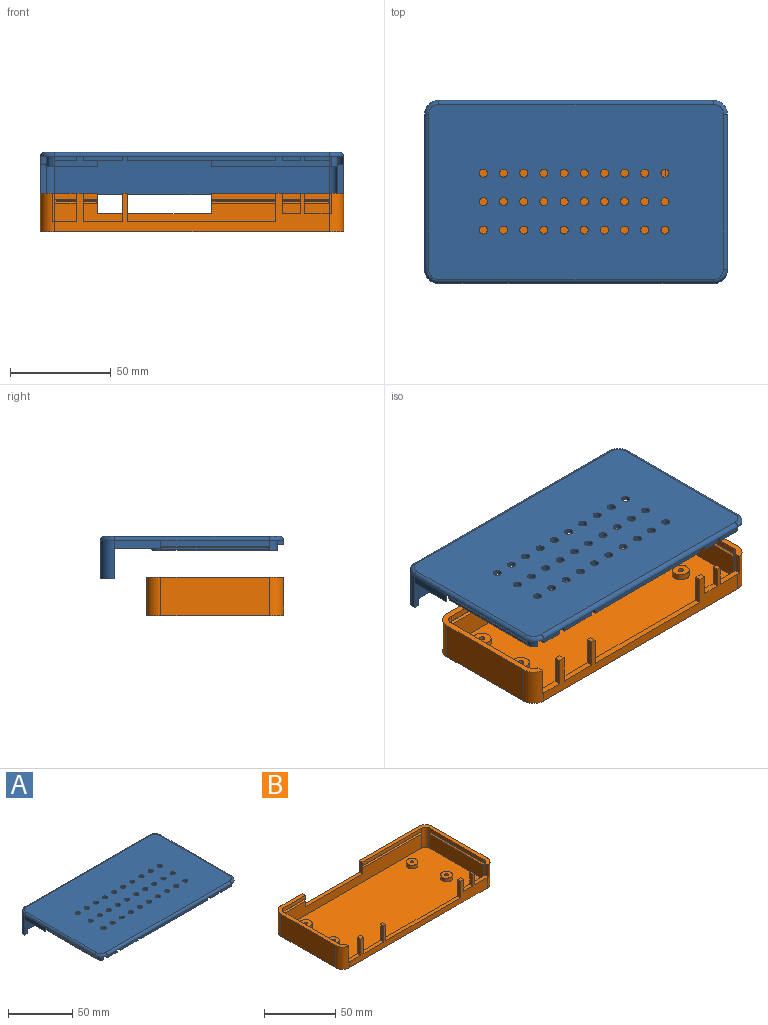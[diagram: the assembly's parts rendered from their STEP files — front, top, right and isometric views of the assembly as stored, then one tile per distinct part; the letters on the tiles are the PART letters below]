
ASSEMBLY  parts=2 mates=1
PART A: 124 faces, bbox 151.4x91.9x21 mm
  f0: plane 12.25x2mm, normal (0,-1,0), area 24.5mm2, adj f74,f75,f76,f118
  f1: plane 8.94x2mm, normal (0,-1,0), area 17.9mm2, adj f82,f83,f84,f118
  f2: plane 73.55x2mm, normal (0,-1,0), area 147.1mm2, adj f66,f67,f68,f118
  f3: plane 19.47x2mm, normal (0,-1,0), area 38.9mm2, adj f70,f71,f72,f118
  f4: plane 23x4mm, normal (-1,0,0), area 92mm2, adj f7,f97,f113,f122
  f5: plane 17.2x4mm, normal (1,0,0), area 68.8mm2, adj f7,f11,f98,f113
  f6: plane 17.2x4mm, normal (-1,0,0), area 68.8mm2, adj f8,f11,f100,f115
  f7: cylinder r=7.1mm len=5.8mm, axis (0,0,1), area 27.1mm2, adj f4,f5,f11,f113
  f8: cylinder r=7.1mm len=5.8mm, axis (0,0,1), area 27.1mm2, adj f6,f11,f13,f115
  f9: plane 53.67x3mm, normal (1,0,0), area 161mm2, adj f11,f47,f48,f91
  f10: plane 53.67x3mm, normal (-1,0,0), area 161mm2, adj f11,f62,f63,f85
  f11: plane 150.25x87.77mm, normal (0,0,-1), area 12041mm2, adj f5,f6,f7,f8,f9,f10,f14,f15
  f12: plane 10.91x2mm, normal (0,-1,0), area 21.8mm2, adj f78,f79,f80,f118
  f13: plane 23x4mm, normal (1,0,0), area 92mm2, adj f8,f95,f115,f117
  f14: cylinder r=2mm len=4mm, axis (0,0,-1), area 25.1mm2, adj f11,f44
  f15: cylinder r=2mm len=4mm, axis (0,0,-1), area 25.1mm2, adj f11,f44
  f16: cylinder r=2mm len=4mm, axis (0,0,-1), area 25.1mm2, adj f11,f44
  f17: cylinder r=2mm len=4mm, axis (0,0,-1), area 25.1mm2, adj f11,f44
  f18: cylinder r=2mm len=4mm, axis (0,0,-1), area 25.1mm2, adj f11,f44
  f19: cylinder r=2mm len=4mm, axis (0,0,-1), area 25.1mm2, adj f11,f44
  f20: cylinder r=2mm len=4mm, axis (0,0,-1), area 25.1mm2, adj f11,f44
  f21: cylinder r=2mm len=4mm, axis (0,0,-1), area 25.1mm2, adj f11,f44
  f22: cylinder r=2mm len=4mm, axis (0,0,-1), area 25.1mm2, adj f11,f44
  f23: cylinder r=2mm len=4mm, axis (0,0,-1), area 25.1mm2, adj f11,f44
  f24: cylinder r=2mm len=4mm, axis (0,0,-1), area 25.1mm2, adj f11,f44
  f25: cylinder r=2mm len=4mm, axis (0,0,-1), area 25.1mm2, adj f11,f44
  f26: cylinder r=2mm len=4mm, axis (0,0,-1), area 25.1mm2, adj f11,f44
  f27: cylinder r=2mm len=4mm, axis (0,0,-1), area 25.1mm2, adj f11,f44
  f28: cylinder r=2mm len=4mm, axis (0,0,-1), area 25.1mm2, adj f11,f44
  f29: cylinder r=2mm len=4mm, axis (0,0,-1), area 25.1mm2, adj f11,f44
  f30: cylinder r=2mm len=4mm, axis (0,0,-1), area 25.1mm2, adj f11,f44
  f31: cylinder r=2mm len=4mm, axis (0,0,-1), area 25.1mm2, adj f11,f44
  f32: cylinder r=2mm len=4mm, axis (0,0,-1), area 25.1mm2, adj f11,f44
  f33: cylinder r=2mm len=4mm, axis (0,0,-1), area 25.1mm2, adj f11,f44
  f34: cylinder r=2mm len=4mm, axis (0,0,-1), area 25.1mm2, adj f11,f44
  f35: cylinder r=2mm len=4mm, axis (0,0,-1), area 25.1mm2, adj f11,f44
  f36: cylinder r=2mm len=4mm, axis (0,0,-1), area 25.1mm2, adj f11,f44
  f37: cylinder r=2mm len=4mm, axis (0,0,-1), area 25.1mm2, adj f11,f44
  f38: cylinder r=2mm len=4mm, axis (0,0,-1), area 25.1mm2, adj f11,f44
  f39: cylinder r=2mm len=4mm, axis (0,0,-1), area 25.1mm2, adj f11,f44
  f40: cylinder r=2mm len=4mm, axis (0,0,-1), area 25.1mm2, adj f11,f44
  f41: cylinder r=2mm len=4mm, axis (0,0,-1), area 25.1mm2, adj f11,f44
  f42: cylinder r=2mm len=4mm, axis (0,0,-1), area 25.1mm2, adj f11,f44
  f43: cylinder r=2mm len=4mm, axis (0,0,-1), area 25.1mm2, adj f11,f44
  f44: plane 146.25x86.77mm, normal (0,0,1), area 12290.9mm2, adj f14,f15,f16,f17,f18,f19,f20,f21
  f45: cylinder r=3mm len=5mm, axis (0,0,1), area 17mm2, adj f11,f46,f53,f54
  f46: plane 5x1.18mm, normal (-1,0,0), area 5.9mm2, adj f11,f45,f47,f54
  f47: cylinder r=4.1mm len=5mm, axis (0,0,1), area 25.7mm2, adj f9,f11,f46,f54,f92
  f48: cylinder r=4.1mm len=5mm, axis (0,0,1), area 32.2mm2, adj f9,f11,f49,f54,f90
  f49: plane 58.46x5mm, normal (0,1,0), area 217.5mm2, adj f11,f48,f50,f54,f103,f104
  f50: plane 5x1.1mm, normal (-1,0,0), area 5.5mm2, adj f11,f49,f51,f54,f102
  f51: plane 58.46x5mm, normal (0,-1,0), area 292.3mm2, adj f11,f50,f52,f54
  f52: cylinder r=3mm len=5mm, axis (0,0,1), area 23.6mm2, adj f11,f51,f53,f54
  f53: plane 53.67x5mm, normal (-1,0,0), area 268.4mm2, adj f11,f45,f52,f54
  f54: plane 62.56x61.67mm, normal (0,0,-1), area 134.2mm2, adj f45,f46,f47,f48,f49,f50,f51,f52
  f55: plane 5x1.14mm, normal (1,0,0), area 5.7mm2, adj f11,f56,f63,f64
  f56: cylinder r=3mm len=5mm, axis (0,0,1), area 18.7mm2, adj f11,f55,f57,f64
  f57: plane 53.67x5mm, normal (1,0,0), area 268.4mm2, adj f11,f56,f58,f64
  f58: cylinder r=3mm len=5mm, axis (0,0,1), area 23.6mm2, adj f11,f57,f59,f64
  f59: plane 21.13x5mm, normal (0,-1,0), area 105.6mm2, adj f11,f58,f60,f64
  f60: plane 5x1.1mm, normal (1,0,0), area 5.5mm2, adj f11,f59,f61,f64
  f61: plane 21.13x5mm, normal (0,1,0), area 74.7mm2, adj f11,f60,f62,f64,f107,f109,f110
  f62: cylinder r=4.1mm len=5mm, axis (0,0,1), area 32.2mm2, adj f10,f11,f61,f64,f86
  f63: cylinder r=4.1mm len=5mm, axis (0,0,1), area 27.4mm2, adj f10,f11,f55,f64,f88
  f64: plane 61.76x25.23mm, normal (0,0,-1), area 93.5mm2, adj f55,f56,f57,f58,f59,f60,f61,f62
  f65: plane 73.55x2mm, normal (0,1,0), area 147.1mm2, adj f11,f66,f67,f68
  f66: plane 3x2mm, normal (-1,0,0), area 6mm2, adj f2,f11,f65,f68
  f67: plane 3x2mm, normal (1,0,0), area 6mm2, adj f2,f11,f65,f68
  f68: plane 73.55x3mm, normal (0,0,-1), area 220.7mm2, adj f2,f65,f66,f67
  f69: plane 19.47x2mm, normal (0,1,0), area 38.9mm2, adj f11,f70,f71,f72
  f70: plane 3x2mm, normal (-1,0,0), area 6mm2, adj f3,f11,f69,f72
  f71: plane 3x2mm, normal (1,0,0), area 6mm2, adj f3,f11,f69,f72
  f72: plane 19.47x3mm, normal (0,0,-1), area 58.4mm2, adj f3,f69,f70,f71
  f73: plane 12.25x2mm, normal (0,1,0), area 24.5mm2, adj f11,f74,f75,f76
  f74: plane 3x2mm, normal (-1,0,0), area 6mm2, adj f0,f11,f73,f76
  f75: plane 3x2mm, normal (1,0,0), area 6mm2, adj f0,f11,f73,f76
  f76: plane 12.25x3mm, normal (0,0,-1), area 36.8mm2, adj f0,f73,f74,f75
  f77: plane 10.91x2mm, normal (0,1,0), area 21.8mm2, adj f11,f78,f79,f80
  f78: plane 3x2mm, normal (-1,0,0), area 6mm2, adj f11,f12,f77,f80
  f79: plane 3x2mm, normal (1,0,0), area 6mm2, adj f11,f12,f77,f80
  f80: plane 10.91x3mm, normal (0,0,-1), area 32.7mm2, adj f12,f77,f78,f79
  f81: plane 8.94x2mm, normal (0,1,0), area 17.9mm2, adj f11,f82,f83,f84
  f82: plane 3x2mm, normal (-1,0,0), area 6mm2, adj f1,f11,f81,f84
  f83: plane 3x2mm, normal (1,0,0), area 6mm2, adj f1,f11,f81,f84
  f84: plane 8.94x3mm, normal (0,0,-1), area 26.8mm2, adj f1,f81,f82,f83
  f85: plane 53.67x0.5mm, normal (-0.64,0,0.77), area 34.8mm2, adj f10,f86,f88,f89
  f86: plane 2x0.5mm, normal (-0.64,0.77,0), area 1mm2, adj f62,f85,f87,f89
  f87: plane 53.67x0.5mm, normal (-0.64,0,-0.77), area 34.8mm2, adj f64,f86,f88,f89
  f88: plane 2x0.5mm, normal (-0.64,-0.77,0), area 1mm2, adj f63,f85,f87,f89
  f89: plane 52.83x1.16mm, normal (-1,0,0), area 61.3mm2, adj f85,f86,f87,f88
  f90: plane 2x0.5mm, normal (0.64,0.77,0), area 1mm2, adj f48,f91,f93,f94
  f91: plane 53.67x0.5mm, normal (0.64,0,0.77), area 34.8mm2, adj f9,f90,f92,f94
  f92: plane 2x0.5mm, normal (0.64,-0.77,0), area 1mm2, adj f47,f91,f93,f94
  f93: plane 53.67x0.5mm, normal (0.64,0,-0.77), area 34.8mm2, adj f54,f90,f92,f94
  f94: plane 52.83x1.16mm, normal (1,0,0), area 61.3mm2, adj f90,f91,f92,f93
  f95: cylinder r=7mm len=19mm, axis (0,0,1), area 208.9mm2, adj f13,f96,f101,f114,f119
  f96: plane 136.25x19mm, normal (0,1,0), area 2588.7mm2, adj f95,f97,f101,f121
  f97: cylinder r=7mm len=19mm, axis (0,0,1), area 208.9mm2, adj f4,f96,f101,f112,f123
  f98: cylinder r=4mm len=19mm, axis (0,0,1), area 119.4mm2, adj f5,f11,f99,f101,f112
  f99: plane 136.25x19mm, normal (0,-1,0), area 2588.7mm2, adj f11,f98,f100,f101
  f100: cylinder r=4mm len=19mm, axis (0,0,1), area 119.4mm2, adj f6,f11,f99,f101,f114
  f101: plane 150.25x7mm, normal (0,0,-1), area 460.6mm2, adj f95,f96,f97,f98,f99,f100,f112,f114
  f102: plane 2x0.5mm, normal (-0.77,0.64,0), area 1mm2, adj f50,f103,f105,f106
  f103: plane 37.38x0.5mm, normal (0,0.64,0.77), area 24.1mm2, adj f49,f102,f104,f106
  f104: plane 2x0.5mm, normal (0.77,0.64,0), area 1mm2, adj f49,f103,f105,f106
  f105: plane 37.38x0.5mm, normal (0,0.64,-0.77), area 24.1mm2, adj f54,f102,f104,f106
  f106: plane 36.54x1.16mm, normal (0,1,0), area 42.4mm2, adj f102,f103,f104,f105
  f107: plane 2x0.5mm, normal (0.77,0.64,0), area 1mm2, adj f61,f108,f110,f111
  f108: plane 15.48x0.5mm, normal (0,0.64,-0.77), area 9.8mm2, adj f64,f107,f109,f111
  f109: plane 2x0.5mm, normal (-0.77,0.64,0), area 1mm2, adj f61,f108,f110,f111
  f110: plane 15.48x0.5mm, normal (0,0.64,0.77), area 9.8mm2, adj f61,f107,f109,f111
  f111: plane 14.64x1.16mm, normal (0,1,0), area 17mm2, adj f107,f108,f109,f110
  f112: plane 15x3mm, normal (0,-1,0), area 45mm2, adj f97,f98,f101,f113
  f113: plane 23x3mm, normal (0,0,-1), area 56.8mm2, adj f4,f5,f7,f112
  f114: plane 15x3mm, normal (0,-1,0), area 45mm2, adj f95,f100,f101,f115
  f115: plane 23x3mm, normal (0,0,-1), area 56.8mm2, adj f6,f8,f13,f114
  f116: torus R=5.1mm, axis (0,0,1), area 31.5mm2, adj f11,f44,f117,f118
  f117: cylinder r=2mm len=76.67mm, axis (0,-1,0), area 240.9mm2, adj f11,f13,f44,f116,f119
  f118: cylinder r=2mm len=136.05mm, axis (-1,0,0), area 427.4mm2, adj f0,f1,f2,f3,f11,f12,f44,f116
  f119: torus R=5mm, axis (0,0,1), area 31mm2, adj f44,f95,f117,f121
  f120: torus R=5.1mm, axis (0,0,1), area 31.5mm2, adj f11,f44,f118,f122
  f121: cylinder r=2mm len=136.25mm, axis (-1,0,0), area 428mm2, adj f44,f96,f119,f123
  f122: cylinder r=2mm len=76.67mm, axis (0,1,0), area 240.9mm2, adj f4,f11,f44,f120,f123
  f123: torus R=5mm, axis (0,0,1), area 31mm2, adj f44,f97,f121,f122
PART B: 78 faces, bbox 150.2x67.9x19 mm
  f0: plane 53.67x12mm, normal (1,0,0), area 644.1mm2, adj f4,f22,f24,f76
  f1: plane 53.67x12mm, normal (-1,0,0), area 644.1mm2, adj f4,f19,f26,f70
  f2: plane 136.05x12mm, normal (0,-1,0), area 1350.2mm2, adj f4,f24,f26,f42,f43,f44,f60,f65
  f3: plane 21.13x3mm, normal (0,-1,0), area 63.4mm2, adj f24,f28,f42,f63
  f4: plane 144.25x61.87mm, normal (0,0,1), area 8687.6mm2, adj f0,f1,f2,f19,f22,f24,f26,f29
  f5: plane 67.76x65.56mm, normal (0,0,1), area 385.3mm2, adj f8,f9,f10,f11,f19,f20,f25,f26
  f6: cylinder r=7.1mm len=19mm, axis (0,0,1), area 198.5mm2, adj f7,f16,f18,f21,f28,f47
  f7: plane 136.05x19mm, normal (0,-1,0), area 917.9mm2, adj f6,f8,f18,f30,f31,f32,f33,f34
  f8: cylinder r=7.1mm len=19mm, axis (0,0,1), area 199.1mm2, adj f5,f7,f9,f18,f20,f45
  f9: plane 53.67x19mm, normal (1,0,0), area 1019.7mm2, adj f5,f8,f10,f18
  f10: cylinder r=7.1mm len=19mm, axis (0,0,1), area 211.9mm2, adj f5,f9,f11,f18
  f11: plane 136.05x19mm, normal (0,1,0), area 2020.2mm2, adj f5,f10,f12,f18,f28,f42,f43,f44
  f12: cylinder r=7.1mm len=19mm, axis (0,0,1), area 211.9mm2, adj f11,f16,f18,f28
  f13: cylinder r=1.25mm len=5mm, axis (0,0,1), area 39.3mm2, adj f18,f53
  f14: cylinder r=1.25mm len=5mm, axis (0,0,1), area 39.3mm2, adj f18,f55
  f15: cylinder r=1.25mm len=5mm, axis (0,0,1), area 39.3mm2, adj f18,f57
  f16: plane 53.67x19mm, normal (-1,0,0), area 1019.7mm2, adj f6,f12,f18,f28
  f17: cylinder r=1.25mm len=5mm, axis (0,0,1), area 39.3mm2, adj f18,f51
  f18: plane 150.25x67.87mm, normal (0,0,-1), area 10134.4mm2, adj f6,f7,f8,f9,f10,f11,f12,f13
  f19: cylinder r=4.1mm len=17mm, axis (0,0,-1), area 96.5mm2, adj f1,f4,f5,f20,f27,f29,f45,f71
  f20: plane 10x3.09mm, normal (-1,0,0), area 30.9mm2, adj f5,f8,f19,f45
  f21: plane 14x3.05mm, normal (1,0,0), area 42.7mm2, adj f6,f22,f28,f47
  f22: cylinder r=4.1mm len=17mm, axis (0,0,-1), area 96mm2, adj f0,f4,f21,f23,f28,f29,f47,f75
  f23: plane 53.67x3mm, normal (1,0,0), area 161mm2, adj f22,f24,f28,f74
  f24: cylinder r=4.1mm len=17mm, axis (0,0,-1), area 109.5mm2, adj f0,f2,f3,f4,f23,f28,f64,f73
  f25: plane 58.46x3mm, normal (0,-1,0), area 175.4mm2, adj f5,f26,f43,f58
  f26: cylinder r=4.1mm len=17mm, axis (0,0,-1), area 109.5mm2, adj f1,f2,f4,f5,f25,f27,f61,f69
  f27: plane 53.67x3mm, normal (-1,0,0), area 161mm2, adj f5,f19,f26,f68
  f28: plane 67.81x28.23mm, normal (0,0,1), area 274.3mm2, adj f3,f6,f11,f12,f16,f21,f22,f23
  f29: plane 136.05x17mm, normal (0,1,0), area 645.8mm2, adj f4,f19,f22,f30,f31,f32,f33,f34
  f30: plane 14x3mm, normal (-1,0,0), area 42mm2, adj f7,f29,f32,f47
  f31: plane 14x3mm, normal (1,0,0), area 42mm2, adj f7,f29,f32,f49
  f32: plane 3.37x3mm, normal (0,0,1), area 10.1mm2, adj f7,f29,f30,f31
  f33: plane 14x3mm, normal (-1,0,0), area 42mm2, adj f7,f29,f35,f48
  f34: plane 10x3mm, normal (1,0,0), area 30mm2, adj f7,f29,f35,f46
  f35: plane 3.36x3mm, normal (0,0,1), area 10.1mm2, adj f7,f29,f33,f34
  f36: plane 14x3mm, normal (-1,0,0), area 42mm2, adj f7,f29,f38,f49
  f37: plane 14x3mm, normal (1,0,0), area 42mm2, adj f7,f29,f38,f48
  f38: plane 3x2.2mm, normal (0,0,1), area 6.6mm2, adj f7,f29,f36,f37
  f39: plane 10x3mm, normal (-1,0,0), area 30mm2, adj f7,f29,f41,f46
  f40: plane 10x3mm, normal (1,0,0), area 30mm2, adj f7,f29,f41,f45
  f41: plane 3x1.99mm, normal (0,0,1), area 6mm2, adj f7,f29,f39,f40
  f42: plane 10x3mm, normal (1,0,0), area 30mm2, adj f2,f3,f11,f28,f44,f66
  f43: plane 10x3mm, normal (-1,0,0), area 30mm2, adj f2,f5,f11,f25,f44,f59
  f44: plane 56.46x3mm, normal (0,0,1), area 169.4mm2, adj f2,f11,f42,f43
  f45: plane 13.53x3.2mm, normal (0,0,1), area 40.6mm2, adj f7,f8,f19,f20,f29,f40
  f46: plane 8.94x3mm, normal (0,0,1), area 26.8mm2, adj f7,f29,f34,f39
  f47: plane 11.87x3.11mm, normal (0,0,1), area 35.6mm2, adj f6,f7,f21,f22,f29,f30
  f48: plane 73.55x3mm, normal (0,0,1), area 220.7mm2, adj f7,f29,f33,f37
  f49: plane 19.47x3mm, normal (0,0,1), area 58.4mm2, adj f7,f29,f31,f36
  f50: cylinder r=4.38mm len=8.76mm, axis (0,0,-1), area 82.5mm2, adj f4,f51
  f51: plane 8.76x8.76mm, normal (0,0,1), area 55.3mm2, adj f17,f50
  f52: cylinder r=4.15mm len=8.3mm, axis (0,0,-1), area 78.2mm2, adj f4,f53
  f53: plane 8.3x8.3mm, normal (0,0,1), area 49.2mm2, adj f13,f52
  f54: cylinder r=4.15mm len=8.3mm, axis (0,0,-1), area 78.2mm2, adj f4,f55
  f55: plane 8.3x8.3mm, normal (0,0,1), area 49.2mm2, adj f14,f54
  f56: cylinder r=4.15mm len=8.3mm, axis (0,0,-1), area 78.2mm2, adj f4,f57
  f57: plane 8.3x8.3mm, normal (0,0,1), area 49.2mm2, adj f15,f56
  f58: plane 58.46x1mm, normal (0,-0.64,-0.77), area 75.2mm2, adj f25,f59,f61,f62
  f59: plane 2x1mm, normal (0.77,-0.64,0), area 1.5mm2, adj f43,f58,f60,f62
  f60: plane 58.46x1mm, normal (0,-0.64,0.77), area 75.2mm2, adj f2,f59,f61,f62
  f61: plane 2x1mm, normal (-0.77,-0.64,0), area 1.5mm2, adj f26,f58,f60,f62
  f62: plane 56.78x0.32mm, normal (0,-1,0), area 18.3mm2, adj f58,f59,f60,f61
  f63: plane 21.13x1mm, normal (0,-0.64,-0.77), area 26.5mm2, adj f3,f64,f66,f67
  f64: plane 2x1mm, normal (0.77,-0.64,0), area 1.5mm2, adj f24,f63,f65,f67
  f65: plane 21.13x1mm, normal (0,-0.64,0.77), area 26.5mm2, adj f2,f64,f66,f67
  f66: plane 2x1mm, normal (-0.77,-0.64,0), area 1.5mm2, adj f42,f63,f65,f67
  f67: plane 19.45x0.32mm, normal (0,-1,0), area 6.3mm2, adj f63,f64,f65,f66
  f68: plane 53.67x1mm, normal (-0.64,0,-0.77), area 69mm2, adj f27,f69,f71,f72
  f69: plane 2x1mm, normal (-0.64,-0.77,0), area 1.5mm2, adj f26,f68,f70,f72
  f70: plane 53.67x1mm, normal (-0.64,0,0.77), area 69mm2, adj f1,f69,f71,f72
  f71: plane 2x1mm, normal (-0.64,0.77,0), area 1.5mm2, adj f19,f68,f70,f72
  f72: plane 51.99x0.32mm, normal (-1,0,0), area 16.7mm2, adj f68,f69,f70,f71
  f73: plane 2x1mm, normal (0.64,-0.77,0), area 1.5mm2, adj f24,f74,f76,f77
  f74: plane 53.67x1mm, normal (0.64,0,-0.77), area 69mm2, adj f23,f73,f75,f77
  f75: plane 2x1mm, normal (0.64,0.77,0), area 1.5mm2, adj f22,f74,f76,f77
  f76: plane 53.67x1mm, normal (0.64,0,0.77), area 69mm2, adj f0,f73,f75,f77
  f77: plane 51.99x0.32mm, normal (1,0,0), area 16.7mm2, adj f73,f74,f75,f76
PLACE A t=(12.26,9.4,35.34)mm
PLACE B t=(-11.28,4.43,0)mm
MATE slider A.f11 <-> B.f32  axis (0,0,-1) through (-45.4,-17.08,35.34)mm
